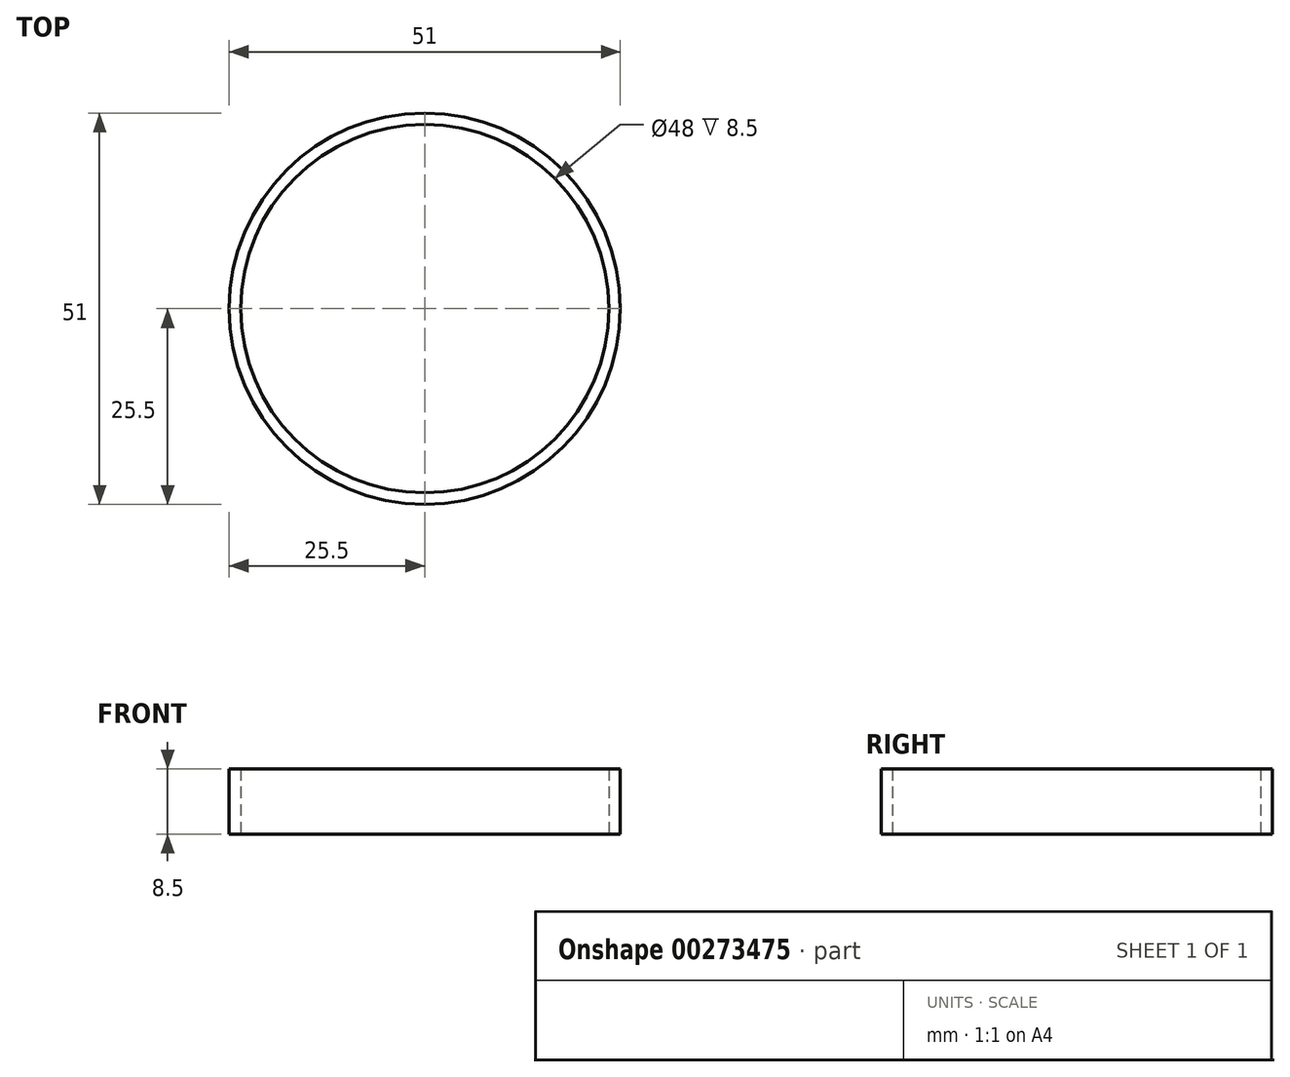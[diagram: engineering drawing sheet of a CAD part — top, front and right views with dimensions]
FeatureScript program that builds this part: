
annotation { "Feature Type Name" : "Feature", "Feature Type Description" : "" }
export const myFeature = defineFeature(function(context is Context, id is Id, definition is map)
    precondition{}
    {
        {
            var Q0;
            Q0=qCreatedBy(makeId("Top.planeOp"),FACE);
            var sketch = newSketch(context, id + "F0", { "sketchPlane" : qUnion([Q0])});
            skCircle(sketch, "E0", {"center": v(0, 0) * mm, "radius": 24 * mm});
            skCircle(sketch, "E1", {"center": v(0, 0) * mm, "radius": 25.5 * mm});
            skSolve(sketch);
        }
        {
            var Q0;
            Q0=makeQuery(id+"F0.imprint","IMPRINT",FACE,{"disambiguationData":[TD([[makeQuery(id+"F0.imprint","IMPRINT",EDGE,{"derivedFrom":sQuery(id+"F0.wireOp",EDGE,"E0")}),-1.0]])]});
            extrude(context, id + "F1", {"entities" : qUnion([Q0]), "depth" : 4.5 * mm});
        }
        {
            var Q0;
            Q0=makeQuery(id+"F1.opExtrude","CAP_FACE",FACE,{"disambiguationData":[OSD([sQuery(id+"F0.wireOp",EDGE,"E0"),sQuery(id+"F0.wireOp",EDGE,"E1")])],"isStart":false});
            extrude(context, id + "F2", {"entities" : qUnion([Q0]), "operationType" : NewBodyOperationType.ADD, "depth" : 4 * mm});
        }
    });
